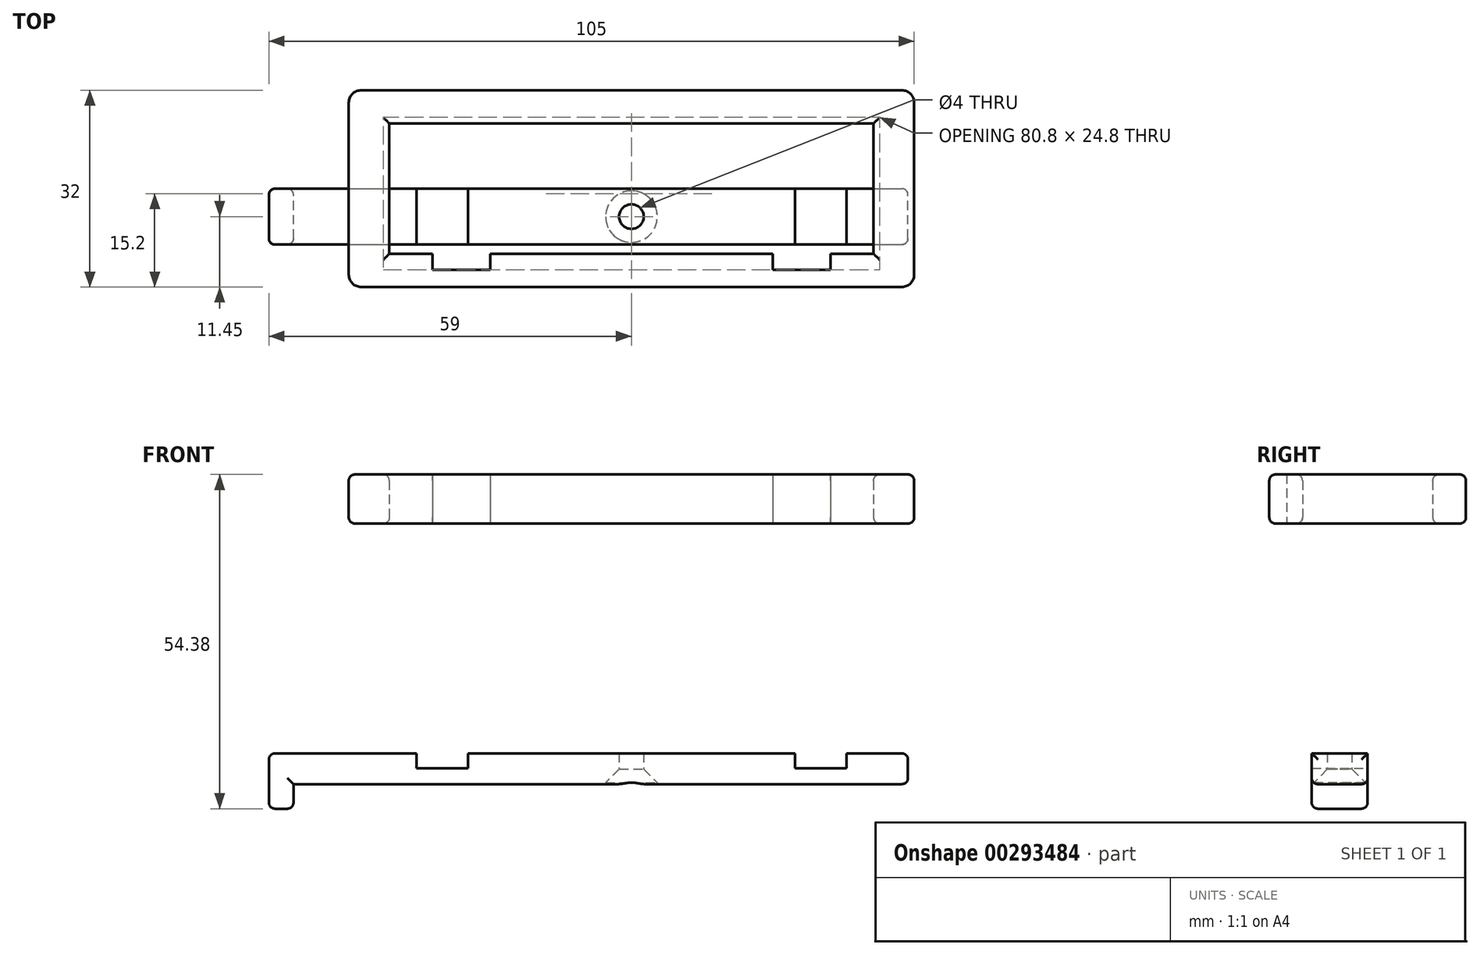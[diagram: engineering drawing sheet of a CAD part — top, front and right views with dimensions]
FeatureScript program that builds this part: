
annotation { "Feature Type Name" : "Feature", "Feature Type Description" : "" }
export const myFeature = defineFeature(function(context is Context, id is Id, definition is map)
    precondition{}
    {
        {
            var Q0;
            Q0=qCreatedBy(makeId("Top.planeOp"),FACE);
            var sketch = newSketch(context, id + "F0", { "sketchPlane" : qUnion([Q0])});
            skLineSegment(sketch, "E0.bottom", {"start": v(39.4, -10.6) * mm, "end": v(32.4, -10.6) * mm});
            skLineSegment(sketch, "E0.left", {"start": v(39.4, -10.6) * mm, "end": v(39.4, 10.6) * mm});
            skLineSegment(sketch, "E0.right", {"start": v(-39.4, -10.6) * mm, "end": v(-39.4, 10.6) * mm});
            skPoint(sketch, "E0.middle", {"position": v(0, 0) * mm});
            skLineSegment(sketch, "E1.bottom", {"start": v(44, -16) * mm, "end": v(-44, -16) * mm});
            skLineSegment(sketch, "E1.top", {"start": v(44, 16) * mm, "end": v(-44, 16) * mm});
            skLineSegment(sketch, "E1.left", {"start": v(46, -14) * mm, "end": v(46, 14) * mm});
            skLineSegment(sketch, "E1.right", {"start": v(-46, -14) * mm, "end": v(-46, 14) * mm});
            skPoint(sketch, "E2.visualSharp", {"position": v(-46, 16) * mm});
            skArc(sketch, "E2.filletArc", {"start": v(-44, 16) * mm, "mid": v(-45.41, 15.41) * mm, "end": v(-46, 14) * mm});
            skPoint(sketch, "E3.visualSharp", {"position": v(46, 16) * mm});
            skArc(sketch, "E3.filletArc", {"start": v(46, 14) * mm, "mid": v(45.41, 15.41) * mm, "end": v(44, 16) * mm});
            skPoint(sketch, "E4.visualSharp", {"position": v(46, -16) * mm});
            skArc(sketch, "E4.filletArc", {"start": v(44, -16) * mm, "mid": v(45.41, -15.41) * mm, "end": v(46, -14) * mm});
            skPoint(sketch, "E5.visualSharp", {"position": v(-46, -16) * mm});
            skArc(sketch, "E5.filletArc", {"start": v(-46, -14) * mm, "mid": v(-45.41, -15.41) * mm, "end": v(-44, -16) * mm});
            skLineSegment(sketch, "E6", {"start": v(-39.4, 10.6) * mm, "end": v(39.4, 10.6) * mm});
            skLineSegment(sketch, "E7", {"start": v(-32.4, -10.6) * mm, "end": v(-32.4, -13.2) * mm});
            skLineSegment(sketch, "E8", {"start": v(-32.4, -13.2) * mm, "end": v(-23, -13.2) * mm});
            skLineSegment(sketch, "E9", {"start": v(-23, -13.2) * mm, "end": v(-23, -10.6) * mm});
            skLineSegment(sketch, "E10.MirrorCS", {"start": v(23, -13.2) * mm, "end": v(23, -10.6) * mm});
            skLineSegment(sketch, "E11.MirrorCS", {"start": v(32.4, -13.2) * mm, "end": v(23, -13.2) * mm});
            skLineSegment(sketch, "E12.MirrorCS", {"start": v(32.4, -10.6) * mm, "end": v(32.4, -13.2) * mm});
            skLineSegment(sketch, "E13.trimOffspring", {"start": v(-32.4, -10.6) * mm, "end": v(-39.4, -10.6) * mm});
            skLineSegment(sketch, "E14.trimOffspring", {"start": v(23, -10.6) * mm, "end": v(-23, -10.6) * mm});
            skSolve(sketch);
        }
        {
            var Q0;
            Q0=makeQuery(id+"F0.imprint","IMPRINT",FACE,{"disambiguationData":[TD([[makeQuery(id+"F0.imprint","IMPRINT",EDGE,{"derivedFrom":sQuery(id+"F0.wireOp",EDGE,"E0.bottom")}),1.0]])]});
            extrude(context, id + "F1", {"entities" : qUnion([Q0]), "depth" : 8 * mm});
        }
        {
            var Q0;
            Q0=qCreatedBy(makeId("Front.planeOp"),FACE);
            var sketch = newSketch(context, id + "F2", { "sketchPlane" : qUnion([Q0])});
            skLineSegment(sketch, "E15.bottom", {"start": v(-45, -42.38) * mm, "end": v(45, -42.38) * mm});
            skLineSegment(sketch, "E15.top", {"start": v(-45, -37.38) * mm, "end": v(-35, -37.38) * mm});
            skLineSegment(sketch, "E15.left", {"start": v(-45, -42.38) * mm, "end": v(-45, -37.38) * mm});
            skLineSegment(sketch, "E15.right", {"start": v(45, -42.38) * mm, "end": v(45, -37.38) * mm});
            skLineSegment(sketch, "E16", {"start": v(-35, -37.38) * mm, "end": v(-35, -39.78) * mm});
            skLineSegment(sketch, "E17", {"start": v(-35, -39.78) * mm, "end": v(-26.6, -39.78) * mm});
            skLineSegment(sketch, "E18", {"start": v(-26.6, -39.78) * mm, "end": v(-26.6, -37.38) * mm});
            skLineSegment(sketch, "E19.MirrorCS", {"start": v(26.6, -39.78) * mm, "end": v(26.6, -37.38) * mm});
            skLineSegment(sketch, "E20.MirrorCS", {"start": v(35, -39.78) * mm, "end": v(26.6, -39.78) * mm});
            skLineSegment(sketch, "E21.MirrorCS", {"start": v(35, -37.38) * mm, "end": v(35, -39.78) * mm});
            skLineSegment(sketch, "E22.trimOffspring", {"start": v(-26.6, -37.38) * mm, "end": v(26.6, -37.38) * mm});
            skLineSegment(sketch, "E23.trimOffspring", {"start": v(35, -37.38) * mm, "end": v(45, -37.38) * mm});
            skLineSegment(sketch, "E24.bottom", {"start": v(-45, -42.38) * mm, "end": v(-55, -42.38) * mm});
            skLineSegment(sketch, "E24.top", {"start": v(-45, -37.38) * mm, "end": v(-55, -37.38) * mm});
            skLineSegment(sketch, "E24.right", {"start": v(-55, -42.38) * mm, "end": v(-55, -37.38) * mm});
            skLineSegment(sketch, "E25.bottom", {"start": v(-55, -37.38) * mm, "end": v(-59, -37.38) * mm});
            skLineSegment(sketch, "E25.top", {"start": v(-55, -46.38) * mm, "end": v(-59, -46.38) * mm});
            skLineSegment(sketch, "E25.left", {"start": v(-55, -37.38) * mm, "end": v(-55, -46.38) * mm});
            skLineSegment(sketch, "E25.right", {"start": v(-59, -37.38) * mm, "end": v(-59, -46.38) * mm});
            skSolve(sketch);
        }
        {
            var Q0;
            Q0=makeQuery(id+"F2.imprint","IMPRINT",FACE,{"disambiguationData":[TD([[makeQuery(id+"F2.imprint","IMPRINT",EDGE,{"derivedFrom":sQuery(id+"F2.wireOp",EDGE,"E15.bottom")}),1.0]])]});
            var Q1;
            {var subQ0=sQuery(id+"F2.wireOp",EDGE,"E24.bottom");Q1=makeQuery(id+"F2.imprint","IMPRINT",FACE,{"disambiguationData":[TD([[makeQuery(id+"F2.imprint","IMPRINT",EDGE,{"derivedFrom":subQ0}),-1.0]])]});}
            var Q2;
            {var subQ3=sQuery(id+"F2.wireOp",EDGE,"rNr5coEB-GTnG-nThL-muiX-QOmL99EaTB1e.bottom");Q2=makeQuery(id+"F2.imprint","IMPRINT",FACE,{"disambiguationData":[TD([[makeQuery(id+"F2.imprint","IMPRINT",EDGE,{"derivedFrom":subQ3}),-1.0]])]});}
            var Q3;
            {var subQ3=sQuery(id+"F2.wireOp",EDGE,"E25.bottom");Q3=makeQuery(id+"F2.imprint","IMPRINT",FACE,{"disambiguationData":[TD([[makeQuery(id+"F2.imprint","IMPRINT",EDGE,{"derivedFrom":subQ3}),1.0]])]});}
            extrude(context, id + "F3", {"entities" : qUnion([Q0, Q1, Q2, Q3]), "depth" : 9.1 * mm});
        }
        {
            var Q0;
            Q0=makeQuery(id+"F1.opExtrude","CAP_EDGE",EDGE,{"disambiguationData":[OSD([sQuery(id+"F0.wireOp",EDGE,"E14.trimOffspring")])],"isStart":true});
            var Q1;
            Q1=makeQuery(id+"F1.opExtrude","CAP_EDGE",EDGE,{"disambiguationData":[OSD([sQuery(id+"F0.wireOp",EDGE,"E0.bottom")])],"isStart":true});
            var Q2;
            Q2=makeQuery(id+"F1.opExtrude","CAP_EDGE",EDGE,{"disambiguationData":[OSD([sQuery(id+"F0.wireOp",EDGE,"E0.bottom")])],"isStart":false});
            var Q3;
            Q3=makeQuery(id+"F1.opExtrude","CAP_EDGE",EDGE,{"disambiguationData":[OSD([sQuery(id+"F0.wireOp",EDGE,"E14.trimOffspring")])],"isStart":false});
            var Q4;
            Q4=makeQuery(id+"F1.opExtrude","CAP_EDGE",EDGE,{"disambiguationData":[OSD([sQuery(id+"F0.wireOp",EDGE,"E13.trimOffspring")])],"isStart":false});
            var Q5;
            Q5=makeQuery(id+"F1.opExtrude","CAP_EDGE",EDGE,{"disambiguationData":[OSD([sQuery(id+"F0.wireOp",EDGE,"E13.trimOffspring")])],"isStart":true});
            fillet(context, id + "F4", {"entities" : qUnion([Q0, Q1, Q2, Q3, Q4, Q5]), "radius" : 1 * mm, "tangentPropagation" : true, "allowEdgeOverflow" : false});
        }
        {
            var Q0;
            Q0=makeQuery(id+"F3.opExtrude","SWEPT_FACE",FACE,{"disambiguationData":[OSD([sQuery(id+"F2.wireOp",EDGE,"E15.bottom")])]});
            var sketch = newSketch(context, id + "F5", { "sketchPlane" : qUnion([Q0])});
            skPoint(sketch, "E26", {"position": v(0, 4.55) * mm});
            skPoint(sketch, "E26.positionSnap0", {"position": v(45, 4.55) * mm});
            skSolve(sketch);
        }
        {
            var Q0;
            Q0=makeQuery(id+"F3.opExtrude","CAP_EDGE",EDGE,{"disambiguationData":[OSD([sQuery(id+"F2.wireOp",EDGE,"E15.bottom")])],"isStart":false});
            var Q1;
            Q1=makeQuery(id+"F3.opExtrude","CAP_EDGE",EDGE,{"disambiguationData":[OSD([sQuery(id+"F2.wireOp",EDGE,"E15.bottom")])],"isStart":true});
            fillet(context, id + "F6", {"entities" : qUnion([Q0, Q1]), "radius" : 1 * mm, "tangentPropagation" : true, "allowEdgeOverflow" : false});
        }
        {
            var Q0;
            Q0=sQuery(id+"F5.wireOp",VERTEX,"E26");
            var Q1;
            Q1=makeQuery(id+"F3.opExtrude","SWEPT_BODY",BODY,{"disambiguationData":[OSD([sQuery(id+"F2.wireOp",EDGE,"E15.bottom"),sQuery(id+"F2.wireOp",EDGE,"E15.top"),sQuery(id+"F2.wireOp",EDGE,"E15.left"),sQuery(id+"F2.wireOp",EDGE,"E15.right"),sQuery(id+"F2.wireOp",EDGE,"E16"),sQuery(id+"F2.wireOp",EDGE,"E17"),sQuery(id+"F2.wireOp",EDGE,"E18"),sQuery(id+"F2.wireOp",EDGE,"E19.MirrorCS"),sQuery(id+"F2.wireOp",EDGE,"E20.MirrorCS"),sQuery(id+"F2.wireOp",EDGE,"E21.MirrorCS"),sQuery(id+"F2.wireOp",EDGE,"E22.trimOffspring"),sQuery(id+"F2.wireOp",EDGE,"E23.trimOffspring")])]});
            hole(context, id + "F7", {"style" : HoleStyle.C_SINK, "endStyle" : HoleEndStyle.THROUGH, "holeDiameter" : 4 * mm, "cSinkDiameter" : 8.4 * mm, "cSinkAngle" : 90 * degree, "tappedDepth" : 12 * mm, "tapClearance" : 3, "locations" : qUnion([Q0]), "scope" : qUnion([Q1])});
        }
        {
            var Q0;
            Q0=makeQuery(id+"F3.opExtrude","SWEPT_EDGE",EDGE,{"disambiguationData":[OSD([sQuery(id+"F2.wireOp",EDGE,"E15.bottom"),sQuery(id+"F2.wireOp",EDGE,"E15.right")])]});
            var Q1;
            Q1=makeQuery(id+"F3.opExtrude","SWEPT_EDGE",EDGE,{"disambiguationData":[OSD([sQuery(id+"F2.wireOp",EDGE,"E15.right"),sQuery(id+"F2.wireOp",EDGE,"E23.trimOffspring")])]});
            fillet(context, id + "F8", {"entities" : qUnion([Q0, Q1]), "radius" : 1 * mm, "tangentPropagation" : true, "allowEdgeOverflow" : false});
        }
        {
            var Q0;
            Q0=makeQuery(id+"F1.opExtrude","CAP_EDGE",EDGE,{"disambiguationData":[OSD([sQuery(id+"F0.wireOp",EDGE,"E6")])],"isStart":true});
            var Q1;
            Q1=makeQuery(id+"F1.opExtrude","CAP_EDGE",EDGE,{"disambiguationData":[OSD([sQuery(id+"F0.wireOp",EDGE,"E6")])],"isStart":false});
            fillet(context, id + "F9", {"entities" : qUnion([Q0, Q1]), "radius" : 1 * mm, "tangentPropagation" : true, "allowEdgeOverflow" : false});
        }
        {
            var Q0;
            Q0=makeQuery(id+"F1.opExtrude","CAP_EDGE",EDGE,{"disambiguationData":[OSD([sQuery(id+"F0.wireOp",EDGE,"E1.left")])],"isStart":true});
            var Q1;
            Q1=makeQuery(id+"F1.opExtrude","CAP_EDGE",EDGE,{"disambiguationData":[OSD([sQuery(id+"F0.wireOp",EDGE,"E1.top")])],"isStart":true});
            var Q2;
            Q2=makeQuery(id+"F1.opExtrude","CAP_EDGE",EDGE,{"disambiguationData":[OSD([sQuery(id+"F0.wireOp",EDGE,"E3.filletArc")])],"isStart":true});
            var Q3;
            Q3=makeQuery(id+"F1.opExtrude","CAP_EDGE",EDGE,{"disambiguationData":[OSD([sQuery(id+"F0.wireOp",EDGE,"E1.right")])],"isStart":true});
            var Q4;
            Q4=makeQuery(id+"F1.opExtrude","CAP_EDGE",EDGE,{"disambiguationData":[OSD([sQuery(id+"F0.wireOp",EDGE,"E2.filletArc")])],"isStart":true});
            var Q5;
            Q5=makeQuery(id+"F1.opExtrude","CAP_EDGE",EDGE,{"disambiguationData":[OSD([sQuery(id+"F0.wireOp",EDGE,"E1.left")])],"isStart":false});
            var Q6;
            Q6=makeQuery(id+"F1.opExtrude","CAP_EDGE",EDGE,{"disambiguationData":[OSD([sQuery(id+"F0.wireOp",EDGE,"E1.top")])],"isStart":false});
            var Q7;
            Q7=makeQuery(id+"F1.opExtrude","CAP_EDGE",EDGE,{"disambiguationData":[OSD([sQuery(id+"F0.wireOp",EDGE,"E3.filletArc")])],"isStart":false});
            var Q8;
            Q8=makeQuery(id+"F1.opExtrude","CAP_EDGE",EDGE,{"disambiguationData":[OSD([sQuery(id+"F0.wireOp",EDGE,"E1.right")])],"isStart":false});
            var Q9;
            Q9=makeQuery(id+"F1.opExtrude","CAP_EDGE",EDGE,{"disambiguationData":[OSD([sQuery(id+"F0.wireOp",EDGE,"E2.filletArc")])],"isStart":false});
            fillet(context, id + "F10", {"entities" : qUnion([Q0, Q1, Q2, Q3, Q4, Q5, Q6, Q7, Q8, Q9]), "radius" : 1 * mm, "tangentPropagation" : true, "allowEdgeOverflow" : false});
        }
        {
            var Q0;
            Q0=makeQuery(id+"F1.opExtrude","CAP_EDGE",EDGE,{"disambiguationData":[OSD([sQuery(id+"F0.wireOp",EDGE,"E0.left")])],"isStart":false});
            var Q1;
            Q1=makeQuery(id+"F1.opExtrude","CAP_EDGE",EDGE,{"disambiguationData":[OSD([sQuery(id+"F0.wireOp",EDGE,"E0.right")])],"isStart":false});
            var Q2;
            Q2=makeQuery(id+"F1.opExtrude","CAP_EDGE",EDGE,{"disambiguationData":[OSD([sQuery(id+"F0.wireOp",EDGE,"E0.right")])],"isStart":true});
            var Q3;
            Q3=makeQuery(id+"F1.opExtrude","CAP_EDGE",EDGE,{"disambiguationData":[OSD([sQuery(id+"F0.wireOp",EDGE,"E0.left")])],"isStart":true});
            fillet(context, id + "F11", {"entities" : qUnion([Q0, Q1, Q2, Q3]), "radius" : 1 * mm, "tangentPropagation" : true, "allowEdgeOverflow" : false});
        }
        {
            var Q0;
            Q0=makeQuery(id+"F3.opExtrude","CAP_EDGE",EDGE,{"disambiguationData":[OSD([sQuery(id+"F2.wireOp",EDGE,"E25.left")])],"isStart":false});
            var Q1;
            Q1=makeQuery(id+"F3.opExtrude","CAP_EDGE",EDGE,{"disambiguationData":[OSD([sQuery(id+"F2.wireOp",EDGE,"E25.top")])],"isStart":false});
            var Q2;
            Q2=makeQuery(id+"F3.opExtrude","CAP_EDGE",EDGE,{"disambiguationData":[OSD([sQuery(id+"F2.wireOp",EDGE,"E25.right")])],"isStart":false});
            var Q3;
            Q3=makeQuery(id+"F3.opExtrude","SWEPT_EDGE",EDGE,{"disambiguationData":[OSD([sQuery(id+"F2.wireOp",EDGE,"E25.top"),sQuery(id+"F2.wireOp",EDGE,"E25.left")])]});
            var Q4;
            Q4=makeQuery(id+"F3.opExtrude","SWEPT_EDGE",EDGE,{"disambiguationData":[OSD([sQuery(id+"F2.wireOp",EDGE,"E25.top"),sQuery(id+"F2.wireOp",EDGE,"E25.right")])]});
            var Q5;
            Q5=makeQuery(id+"F3.opExtrude","CAP_EDGE",EDGE,{"disambiguationData":[OSD([sQuery(id+"F2.wireOp",EDGE,"E25.top")])],"isStart":true});
            var Q6;
            Q6=makeQuery(id+"F3.opExtrude","CAP_EDGE",EDGE,{"disambiguationData":[OSD([sQuery(id+"F2.wireOp",EDGE,"E25.left")])],"isStart":true});
            var Q7;
            Q7=makeQuery(id+"F3.opExtrude","CAP_EDGE",EDGE,{"disambiguationData":[OSD([sQuery(id+"F2.wireOp",EDGE,"E25.right")])],"isStart":true});
            var Q8;
            Q8=makeQuery(id+"F3.opExtrude","SWEPT_EDGE",EDGE,{"disambiguationData":[OSD([sQuery(id+"F2.wireOp",EDGE,"E25.bottom"),sQuery(id+"F2.wireOp",EDGE,"E25.right")])]});
            fillet(context, id + "F12", {"entities" : qUnion([Q0, Q1, Q2, Q3, Q4, Q5, Q6, Q7, Q8]), "radius" : 1 * mm, "tangentPropagation" : true, "allowEdgeOverflow" : false});
        }
    });
